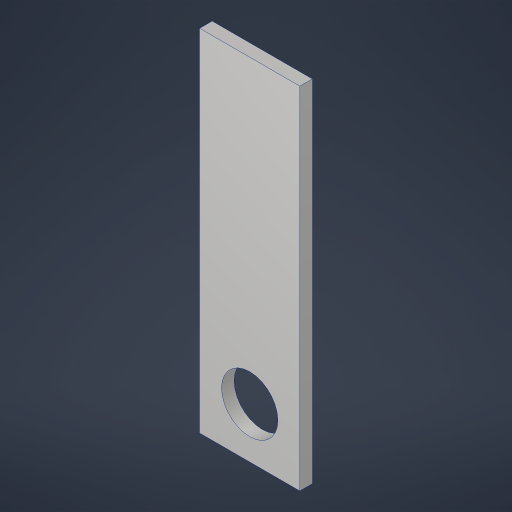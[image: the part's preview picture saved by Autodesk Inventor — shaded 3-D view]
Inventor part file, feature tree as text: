
AUTODESK INVENTOR PART (.ipt)
format: ipt  version: 2023.4 (Build 274418000, 418)  size: 178,688 bytes
history: native  units: in
note: dims shown in document units (in); Inventor stores cm internally (conversion verified against a paired STEP export)
features: extrude x1, hole x1, sketch x1, projected_geometry x1
ambient origin geometry x8: Origin, YZ Plane, XZ Plane, XY Plane, X Axis, Y Axis, Z Axis, Center Point
bodies: Solid1 (feature_tree)
feature tree (4):
  extrude  "Extrusion1"  Depth=0.25in
  hole  "Hole1"  [1 undecoded]
  sketch  "Sketch2"  dims[d3=0.0in d4=1.0in d5=1.125in d6=0.75in d7=0.385in d8=0.25in d9=0.5635in d10=1.0in d11=0.8108in]
  projected_geometry  "Project Cut Edges1"
note: 1 required parameter value undecoded (feature->parameter linkage not recoverable at this tier; creation-order binding heuristic only, values carry confidence <= 0.55)
